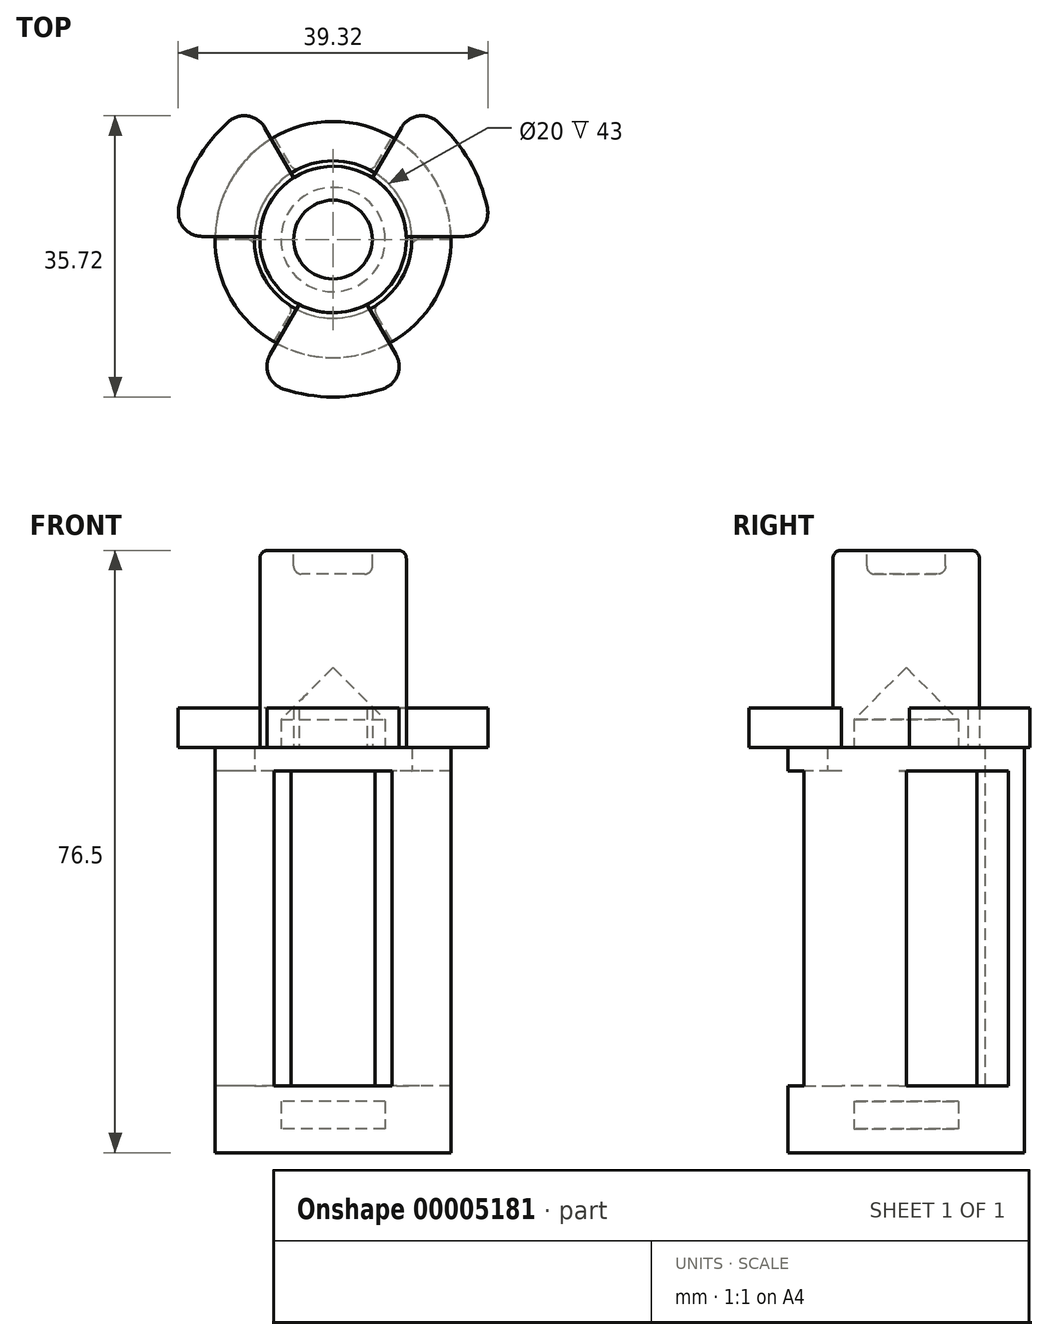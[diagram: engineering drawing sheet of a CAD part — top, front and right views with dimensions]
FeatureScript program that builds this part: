
annotation { "Feature Type Name" : "Feature", "Feature Type Description" : "" }
export const myFeature = defineFeature(function(context is Context, id is Id, definition is map)
    precondition{}
    {
        {
            var Q0;
            Q0=qCreatedBy(makeId("Top.planeOp"),FACE);
            var sketch = newSketch(context, id + "F0", { "sketchPlane" : qUnion([Q0])});
            skCircle(sketch, "E0", {"center": v(0, 0) * mm, "radius": 15 * mm});
            skSolve(sketch);
        }
        {
            var Q0;
            Q0 = qSketchRegion(id + "F0", true);
            extrude(context, id + "F1", {"entities" : qUnion([Q0]), "depth" : 3 * mm});
        }
        {
            var Q0;
            Q0=makeQuery(id+"F1.opExtrude","CAP_FACE",FACE,{"disambiguationData":[OSD([sQuery(id+"F0.wireOp",EDGE,"E0")])],"isStart":false});
            var sketch = newSketch(context, id + "F2", { "sketchPlane" : qUnion([Q0])});
            skCircle(sketch, "E1", {"center": v(0, 0) * mm, "radius": 6.62 * mm});
            skCircle(sketch, "E2.0", {"center": v(0, 0) * mm, "radius": 15 * mm});
            skSolve(sketch);
        }
        {
            var Q0;
            Q0 = qSketchRegion(id + "F2", true);
            extrude(context, id + "F3", {"entities" : qUnion([Q0]), "operationType" : NewBodyOperationType.ADD, "depth" : 3.5 * mm});
        }
        {
            var Q0;
            Q0=makeQuery(id+"F3.opExtrude","CAP_FACE",FACE,{"disambiguationData":[OSD([sQuery(id+"F2.wireOp",EDGE,"E1"),sQuery(id+"F2.wireOp",EDGE,"E2.0")])],"isStart":false});
            var sketch = newSketch(context, id + "F4", { "sketchPlane" : qUnion([Q0])});
            skCircle(sketch, "E3.0", {"center": v(0, 0) * mm, "radius": 15 * mm});
            skSolve(sketch);
        }
        {
            var Q0;
            Q0 = qSketchRegion(id + "F4", true);
            extrude(context, id + "F5", {"entities" : qUnion([Q0]), "operationType" : NewBodyOperationType.ADD, "depth" : 2 * mm});
        }
        {
            var Q0;
            Q0=makeQuery(id+"F5.opExtrude","CAP_FACE",FACE,{"disambiguationData":[OSD([sQuery(id+"F4.wireOp",EDGE,"E3.0")])],"isStart":false});
            var sketch = newSketch(context, id + "F6", { "sketchPlane" : qUnion([Q0])});
            skSolve(sketch);
        }
        {
            var Q0;
            Q0=makeQuery(id+"F6.imprint","IMPRINT",FACE,{"disambiguationData":[TD([[makeQuery(id+"F6.imprint","IMPRINT",EDGE,{"derivedFrom":makeQuery(id+"F5.opExtrude","CAP_EDGE",EDGE,{"disambiguationData":[OSD([sQuery(id+"F4.wireOp",EDGE,"E3.0")])],"isStart":false})}),1.0]])]});
            var sketch = newSketch(context, id + "F7", { "sketchPlane" : qUnion([Q0])});
            skLineSegment(sketch, "E4", {"start": v(0, 0) * mm, "end": v(0, 15) * mm, "construction": true});
            skArc(sketch, "E5", {"start": v(-7.5, 13) * mm, "mid": v(0, 15) * mm, "end": v(7.5, 13) * mm});
            skArc(sketch, "E6", {"start": v(-5, 8.66) * mm, "mid": v(0, 10) * mm, "end": v(5, 8.66) * mm});
            skLineSegment(sketch, "E7", {"start": v(-7.5, 13) * mm, "end": v(-5, 8.66) * mm});
            skLineSegment(sketch, "E8", {"start": v(5, 8.66) * mm, "end": v(7.5, 13) * mm});
            skLineSegment(sketch, "E9", {"start": v(-5, 8.66) * mm, "end": v(0, 0) * mm, "construction": true});
            skArc(sketch, "E10.1.0", {"start": v(-7.5, -13) * mm, "mid": v(-13, -7.5) * mm, "end": v(-15, 0) * mm});
            skLineSegment(sketch, "E10.1.1", {"start": v(-7.5, -13) * mm, "end": v(-5, -8.66) * mm});
            skArc(sketch, "E10.1.2", {"start": v(-5, -8.66) * mm, "mid": v(-8.66, -5) * mm, "end": v(-10, 0) * mm});
            skLineSegment(sketch, "E10.1.3", {"start": v(-10, 0) * mm, "end": v(-15, 0) * mm});
            skArc(sketch, "E10.2.0", {"start": v(15, 0) * mm, "mid": v(13, -7.5) * mm, "end": v(7.5, -13) * mm});
            skLineSegment(sketch, "E10.2.1", {"start": v(15, 0) * mm, "end": v(10, 0) * mm});
            skArc(sketch, "E10.2.2", {"start": v(10, 0) * mm, "mid": v(8.66, -5) * mm, "end": v(5, -8.66) * mm});
            skLineSegment(sketch, "E10.2.3", {"start": v(5, -8.66) * mm, "end": v(7.5, -13) * mm});
            skSolve(sketch);
        }
        {
            var Q0;
            Q0 = qSketchRegion(id + "F7", true);
            extrude(context, id + "F8", {"entities" : qUnion([Q0]), "operationType" : NewBodyOperationType.ADD, "depth" : 40 * mm});
        }
        {
            var Q0;
            Q0=makeQuery(id+"F8.opExtrude","CAP_FACE",FACE,{"disambiguationData":[OSD([sQuery(id+"F7.wireOp",EDGE,"E5"),sQuery(id+"F7.wireOp",EDGE,"E6"),sQuery(id+"F7.wireOp",EDGE,"E7"),sQuery(id+"F7.wireOp",EDGE,"E8")])],"isStart":false});
            var sketch = newSketch(context, id + "F9", { "sketchPlane" : qUnion([Q0])});
            skCircle(sketch, "E11", {"center": v(0, 0) * mm, "radius": 15 * mm});
            skCircle(sketch, "E12", {"center": v(0, 0) * mm, "radius": 10 * mm});
            skSolve(sketch);
        }
        {
            var Q0;
            Q0 = qSketchRegion(id + "F9", true);
            extrude(context, id + "F10", {"entities" : qUnion([Q0]), "operationType" : NewBodyOperationType.ADD, "depth" : 3 * mm});
        }
        {
            var Q0;
            Q0=makeQuery(id+"F8.opExtrude","SWEPT_EDGE",EDGE,{"disambiguationData":[OSD([sQuery(id+"F7.wireOp",EDGE,"E10.1.1"),sQuery(id+"F7.wireOp",EDGE,"E10.1.2")])]});
            var Q1;
            Q1=makeQuery(id+"F8.opExtrude","SWEPT_EDGE",EDGE,{"disambiguationData":[OSD([sQuery(id+"F7.wireOp",EDGE,"E10.1.2"),sQuery(id+"F7.wireOp",EDGE,"E10.1.3")])]});
            var Q2;
            Q2=makeQuery(id+"F8.opExtrude","SWEPT_EDGE",EDGE,{"disambiguationData":[OSD([sQuery(id+"F7.wireOp",EDGE,"E6"),sQuery(id+"F7.wireOp",EDGE,"E7")])]});
            var Q3;
            Q3=makeQuery(id+"F8.opExtrude","SWEPT_EDGE",EDGE,{"disambiguationData":[OSD([sQuery(id+"F7.wireOp",EDGE,"E6"),sQuery(id+"F7.wireOp",EDGE,"E8")])]});
            var Q4;
            Q4=makeQuery(id+"F8.opExtrude","SWEPT_EDGE",EDGE,{"disambiguationData":[OSD([sQuery(id+"F7.wireOp",EDGE,"E10.2.2"),sQuery(id+"F7.wireOp",EDGE,"E10.2.3")])]});
            var Q5;
            Q5=makeQuery(id+"F8.opExtrude","SWEPT_EDGE",EDGE,{"disambiguationData":[OSD([sQuery(id+"F7.wireOp",EDGE,"E10.2.1"),sQuery(id+"F7.wireOp",EDGE,"E10.2.2")])]});
            fillet(context, id + "F11", {"entities" : qUnion([Q0, Q1, Q2, Q3, Q4, Q5]), "radius" : 1 * mm, "tangentPropagation" : true, "allowEdgeOverflow" : false});
        }
        {
            var Q0;
            Q0=makeQuery(id+"F10.opExtrude","CAP_FACE",FACE,{"disambiguationData":[OSD([sQuery(id+"F9.wireOp",EDGE,"E11"),sQuery(id+"F9.wireOp",EDGE,"E12")])],"isStart":false});
            var sketch = newSketch(context, id + "F12", { "sketchPlane" : qUnion([Q0])});
            skLineSegment(sketch, "E13.0", {"start": v(-7.5, 13) * mm, "end": v(-5.48, 9.49) * mm, "construction": true});
            skLineSegment(sketch, "E13.1", {"start": v(5.48, 9.49) * mm, "end": v(7.5, 13) * mm, "construction": true});
            skCircle(sketch, "E14", {"center": v(0, 0) * mm, "radius": 9.3 * mm});
            skSolve(sketch);
        }
        {
            var Q0;
            Q0 = qSketchRegion(id + "F12", true);
            extrude(context, id + "F13", {"entities" : qUnion([Q0]), "depth" : 25 * mm});
        }
        {
            var Q0;
            Q0=makeQuery(id+"F13.opExtrude","CAP_FACE",FACE,{"disambiguationData":[OSD([sQuery(id+"F12.wireOp",EDGE,"E14")])],"isStart":true});
            var sketch = newSketch(context, id + "F14", { "sketchPlane" : qUnion([Q0])});
            skCircle(sketch, "E15", {"center": v(0, 0) * mm, "radius": 6.62 * mm});
            skSolve(sketch);
        }
        {
            var Q0;
            Q0 = qSketchRegion(id + "F14", true);
            extrude(context, id + "F15", {"entities" : qUnion([Q0]), "operationType" : NewBodyOperationType.REMOVE, "oppositeDirection" : true, "depth" : (3.5 + 13.25 / 2) * mm});
        }
        {
            var Q0;
            Q0=makeQuery(id+"F13.opExtrude","CAP_FACE",FACE,{"disambiguationData":[OSD([sQuery(id+"F12.wireOp",EDGE,"E14")])],"isStart":true});
            var sketch = newSketch(context, id + "F16", { "sketchPlane" : qUnion([Q0])});
            skLineSegment(sketch, "E16.0", {"start": v(-7.5, 13) * mm, "end": v(-5.48, 9.49) * mm, "construction": true});
            skLineSegment(sketch, "E16.1", {"start": v(5.48, 9.49) * mm, "end": v(7.5, 13) * mm, "construction": true});
            skCircle(sketch, "E17.0", {"center": v(0, 0) * mm, "radius": 9.3 * mm, "construction": true});
            skLineSegment(sketch, "E18", {"start": v(0, 0) * mm, "end": v(0, 17.93) * mm, "construction": true});
            skArc(sketch, "E19", {"start": v(-4.3, 8.25) * mm, "mid": v(0, 9.3) * mm, "end": v(4.3, 8.25) * mm});
            skLineSegment(sketch, "E20", {"start": v(-4.3, 8.25) * mm, "end": v(-9.65, 17.52) * mm});
            skLineSegment(sketch, "E21.MirrorCS", {"start": v(4.3, 8.25) * mm, "end": v(9.65, 17.52) * mm});
            skArc(sketch, "E22", {"start": v(-9.65, 17.52) * mm, "mid": v(0, 20) * mm, "end": v(9.65, 17.52) * mm});
            skArc(sketch, "E23.1.0", {"start": v(-10.34, -17.12) * mm, "mid": v(-17.32, -10) * mm, "end": v(-20, -0.4) * mm});
            skLineSegment(sketch, "E23.1.1", {"start": v(-9.3, -0.4) * mm, "end": v(-20, -0.4) * mm});
            skLineSegment(sketch, "E23.1.2", {"start": v(-5, -7.85) * mm, "end": v(-10.34, -17.12) * mm});
            skArc(sketch, "E23.1.3", {"start": v(-5, -7.85) * mm, "mid": v(-8.05, -4.65) * mm, "end": v(-9.3, -0.4) * mm});
            skArc(sketch, "E23.2.0", {"start": v(20, -0.4) * mm, "mid": v(17.32, -10) * mm, "end": v(10.34, -17.12) * mm});
            skLineSegment(sketch, "E23.2.1", {"start": v(5, -7.85) * mm, "end": v(10.34, -17.12) * mm});
            skLineSegment(sketch, "E23.2.2", {"start": v(9.3, -0.4) * mm, "end": v(20, -0.4) * mm});
            skArc(sketch, "E23.2.3", {"start": v(9.3, -0.4) * mm, "mid": v(8.05, -4.65) * mm, "end": v(5, -7.85) * mm});
            skSolve(sketch);
        }
        {
            var Q0;
            Q0 = qSketchRegion(id + "F16", true);
            extrude(context, id + "F17", {"entities" : qUnion([Q0]), "operationType" : NewBodyOperationType.ADD, "oppositeDirection" : true, "depth" : 5 * mm});
        }
        {
            var Q0;
            Q0=makeQuery(id+"F17.opExtrude","SWEPT_EDGE",EDGE,{"disambiguationData":[OSD([sQuery(id+"F16.wireOp",EDGE,"E20"),sQuery(id+"F16.wireOp",EDGE,"E22")])]});
            var Q1;
            Q1=makeQuery(id+"F17.opExtrude","SWEPT_EDGE",EDGE,{"disambiguationData":[OSD([sQuery(id+"F16.wireOp",EDGE,"E21.MirrorCS"),sQuery(id+"F16.wireOp",EDGE,"E22")])]});
            var Q2;
            Q2=makeQuery(id+"F17.opExtrude","SWEPT_EDGE",EDGE,{"disambiguationData":[OSD([sQuery(id+"F16.wireOp",EDGE,"E23.1.0"),sQuery(id+"F16.wireOp",EDGE,"E23.1.1")])]});
            var Q3;
            Q3=makeQuery(id+"F17.opExtrude","SWEPT_EDGE",EDGE,{"disambiguationData":[OSD([sQuery(id+"F16.wireOp",EDGE,"E23.1.0"),sQuery(id+"F16.wireOp",EDGE,"E23.1.2")])]});
            var Q4;
            Q4=makeQuery(id+"F17.opExtrude","SWEPT_EDGE",EDGE,{"disambiguationData":[OSD([sQuery(id+"F16.wireOp",EDGE,"E23.2.0"),sQuery(id+"F16.wireOp",EDGE,"E23.2.1")])]});
            var Q5;
            Q5=makeQuery(id+"F17.opExtrude","SWEPT_EDGE",EDGE,{"disambiguationData":[OSD([sQuery(id+"F16.wireOp",EDGE,"E23.2.0"),sQuery(id+"F16.wireOp",EDGE,"E23.2.2")])]});
            fillet(context, id + "F18", {"entities" : qUnion([Q0, Q1, Q2, Q3, Q4, Q5]), "radius" : 3 * mm, "tangentPropagation" : true, "allowEdgeOverflow" : false});
        }
        {
            var Q0;
            Q0=makeQuery(id+"F15.boolean.opBoolean","COPY",EDGE,{"derivedFrom":makeQuery(id+"F15.opExtrude","CAP_EDGE",EDGE,{"disambiguationData":[OSD([sQuery(id+"F14.wireOp",EDGE,"E15")])],"isStart":false})});
            chamfer(context, id + "F19", {"entities" : qUnion([Q0]), "width" : (13.25 / 2) * mm, "tangentPropagation" : true});
        }
        {
            var Q0;
            Q0=makeQuery(id+"F13.opExtrude","CAP_FACE",FACE,{"disambiguationData":[OSD([sQuery(id+"F12.wireOp",EDGE,"E14")])],"isStart":false});
            var sketch = newSketch(context, id + "F20", { "sketchPlane" : qUnion([Q0])});
            skCircle(sketch, "E24", {"center": v(0, 0) * mm, "radius": 5 * mm});
            skSolve(sketch);
        }
        {
            var Q0;
            Q0 = qSketchRegion(id + "F20", true);
            extrude(context, id + "F21", {"entities" : qUnion([Q0]), "operationType" : NewBodyOperationType.REMOVE, "oppositeDirection" : true, "depth" : 3 * mm});
        }
        {
            var Q0;
            Q0=makeQuery(id+"F13.opExtrude","CAP_EDGE",EDGE,{"disambiguationData":[OSD([sQuery(id+"F12.wireOp",EDGE,"E14")])],"isStart":false});
            var Q1;
            Q1=makeQuery(id+"F21.boolean.opBoolean","COPY",EDGE,{"derivedFrom":makeQuery(id+"F21.opExtrude","CAP_EDGE",EDGE,{"disambiguationData":[OSD([sQuery(id+"F20.wireOp",EDGE,"E24")])],"isStart":false})});
            fillet(context, id + "F22", {"entities" : qUnion([Q0, Q1]), "radius" : 1 * mm, "tangentPropagation" : true, "allowEdgeOverflow" : false});
        }
    });
